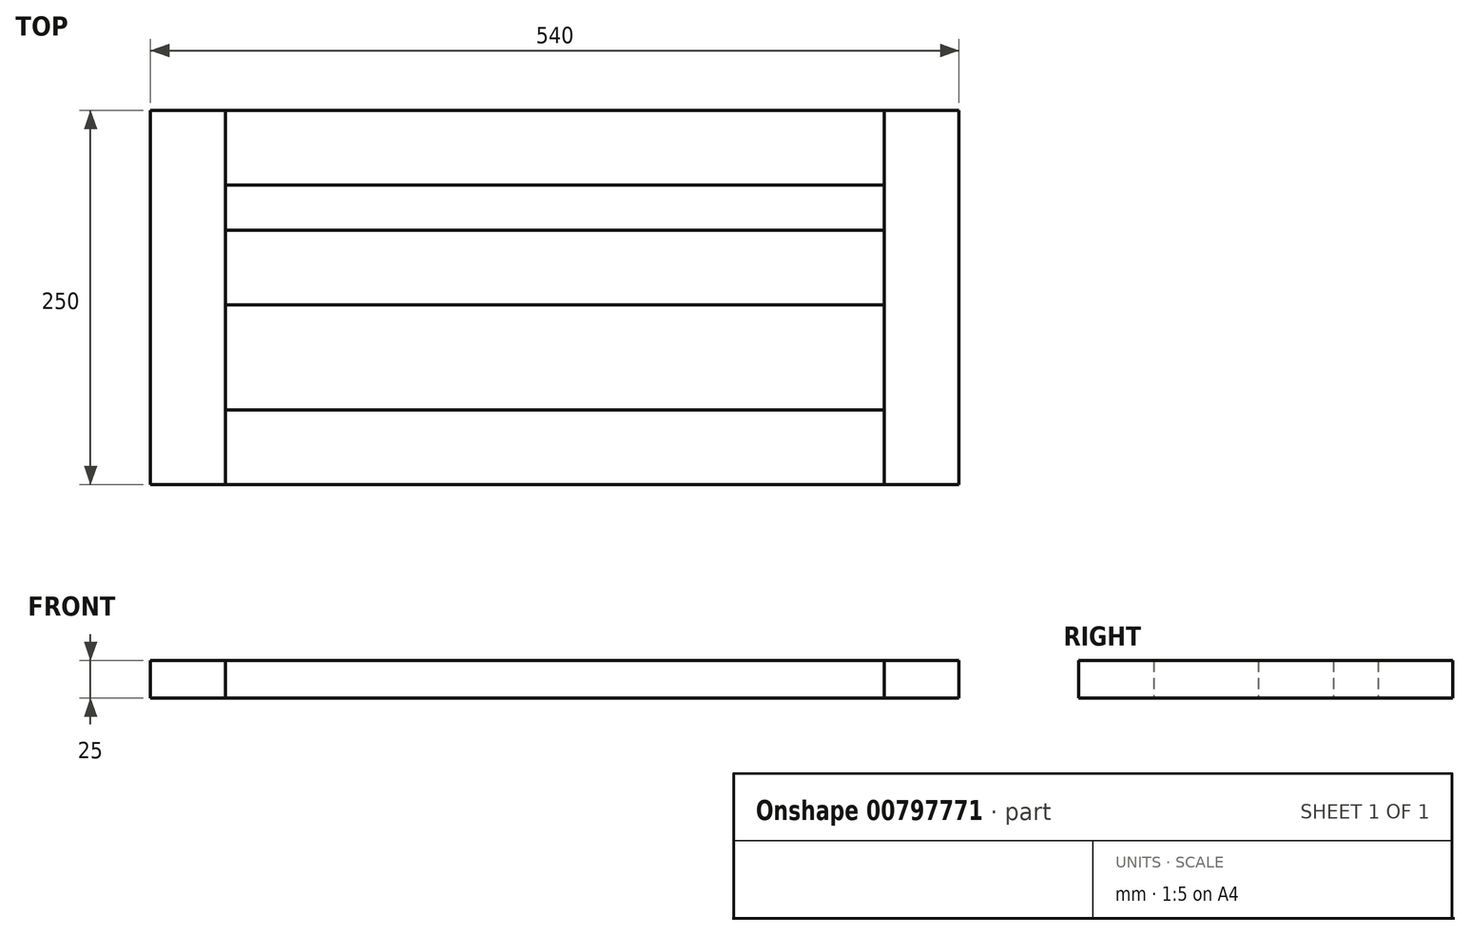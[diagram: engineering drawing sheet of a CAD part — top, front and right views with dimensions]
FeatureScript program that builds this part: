
annotation { "Feature Type Name" : "Feature", "Feature Type Description" : "" }
export const myFeature = defineFeature(function(context is Context, id is Id, definition is map)
    precondition{}
    {
        {
            var Q0;
            Q0=qCreatedBy(makeId("Top.planeOp"),FACE);
            var sketch = newSketch(context, id + "F0", { "sketchPlane" : qUnion([Q0])});
            skLineSegment(sketch, "E0.bottom", {"start": v(220, -25) * mm, "end": v(-220, -25) * mm});
            skLineSegment(sketch, "E0.top", {"start": v(220, 25) * mm, "end": v(-220, 25) * mm});
            skLineSegment(sketch, "E0.left", {"start": v(220, -25) * mm, "end": v(220, 25) * mm});
            skLineSegment(sketch, "E0.right", {"start": v(-220, -25) * mm, "end": v(-220, 25) * mm});
            skPoint(sketch, "E0.middle", {"position": v(0, 0) * mm});
            skSolve(sketch);
        }
        {
            var Q0;
            Q0 = qSketchRegion(id + "F0", true);
            extrude(context, id + "F1", {"entities" : qUnion([Q0]), "depth" : 25 * mm, "offsetDistance" : 25 * mm});
        }
        {
            var Q0;
            Q0=qCreatedBy(makeId("Front.planeOp"),FACE);
            var sketch = newSketch(context, id + "F2", { "sketchPlane" : qUnion([Q0])});
            skLineSegment(sketch, "E1.bottom", {"start": v(220, 25) * mm, "end": v(270, 25) * mm});
            skLineSegment(sketch, "E1.top", {"start": v(220, 0) * mm, "end": v(270, 0) * mm});
            skLineSegment(sketch, "E1.left", {"start": v(220, 25) * mm, "end": v(220, 0) * mm});
            skLineSegment(sketch, "E1.right", {"start": v(270, 25) * mm, "end": v(270, 0) * mm});
            skSolve(sketch);
        }
        {
            var Q0;
            Q0=makeQuery(id+"F2.imprint","IMPRINT",FACE,{"disambiguationData":[TD([[makeQuery(id+"F2.imprint","IMPRINT",EDGE,{"derivedFrom":sQuery(id+"F2.wireOp",EDGE,"E1.bottom")}),-1.0]])]});
            extrude(context, id + "F3", {"entities" : qUnion([Q0]), "oppositeDirection" : true, "depth" : 225 * mm, "offsetDistance" : 25 * mm, "hasSecondDirection" : true, "secondDirectionOppositeDirection" : false, "secondDirectionDepth" : 25 * mm});
        }
        {
            var Q0;
            Q0=makeQuery(id+"F3.opExtrude","SWEPT_BODY",BODY,{"disambiguationData":[OSD([sQuery(id+"F2.wireOp",EDGE,"E1.bottom"),sQuery(id+"F2.wireOp",EDGE,"E1.top"),sQuery(id+"F2.wireOp",EDGE,"E1.left"),sQuery(id+"F2.wireOp",EDGE,"E1.right")])]});
            transform(context, id + "F4", {"entities" : qUnion([Q0]), "transformType" : TransformType.TRANSLATION_3D, "dx" : -490 * mm, "dy" : 0 * mm, "dz" : 0 * mm, "makeCopy" : true});
        }
        {
            var Q0;
            Q0=makeQuery(id+"F1.opExtrude","SWEPT_BODY",BODY,{"disambiguationData":[OSD([sQuery(id+"F0.wireOp",EDGE,"E0.bottom"),sQuery(id+"F0.wireOp",EDGE,"E0.top"),sQuery(id+"F0.wireOp",EDGE,"E0.left"),sQuery(id+"F0.wireOp",EDGE,"E0.right")])]});
            transform(context, id + "F5", {"entities" : qUnion([Q0]), "transformType" : TransformType.TRANSLATION_3D, "dx" : 0 * mm, "dy" : 200 * mm, "dz" : 0 * mm, "makeCopy" : true});
        }
        {
            var Q0;
            Q0=makeQuery(id+"F1.opExtrude","SWEPT_BODY",BODY,{"disambiguationData":[OSD([sQuery(id+"F0.wireOp",EDGE,"E0.bottom"),sQuery(id+"F0.wireOp",EDGE,"E0.top"),sQuery(id+"F0.wireOp",EDGE,"E0.left"),sQuery(id+"F0.wireOp",EDGE,"E0.right")])]});
            transform(context, id + "F6", {"entities" : qUnion([Q0]), "transformType" : TransformType.TRANSLATION_3D, "dx" : 0 * mm, "dy" : 120 * mm, "dz" : 0 * mm, "makeCopy" : true});
        }
    });
